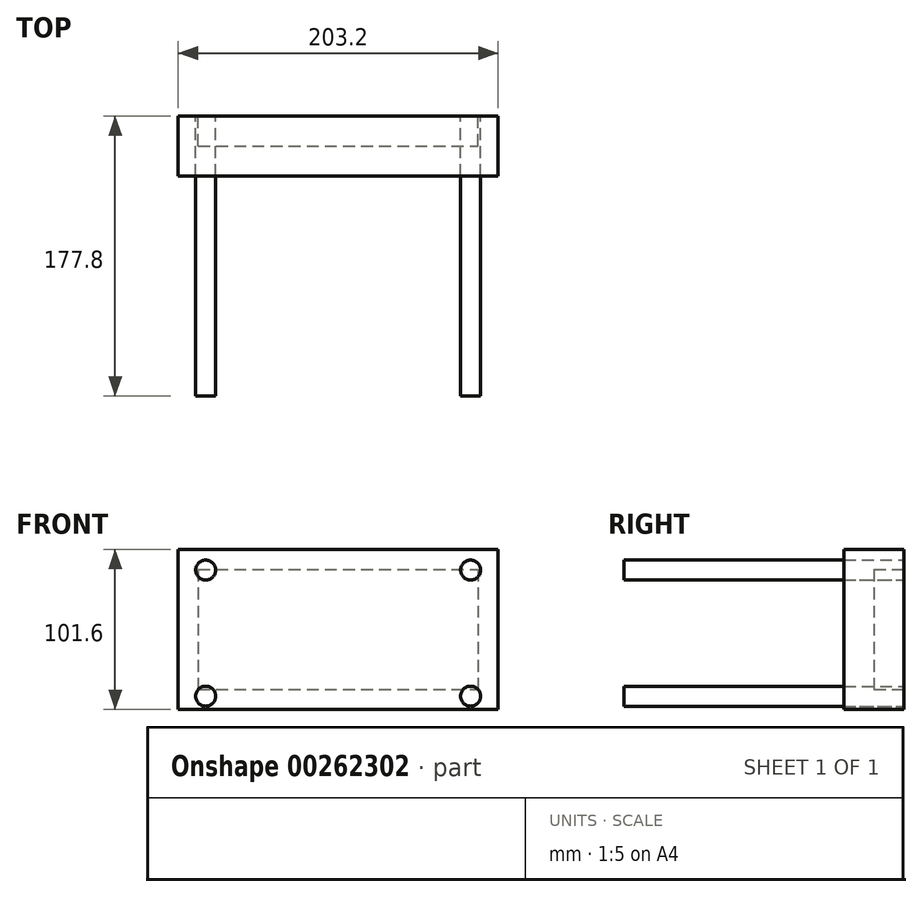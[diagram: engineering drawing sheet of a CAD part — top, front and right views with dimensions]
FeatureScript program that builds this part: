
annotation { "Feature Type Name" : "Feature", "Feature Type Description" : "" }
export const myFeature = defineFeature(function(context is Context, id is Id, definition is map)
    precondition{}
    {
        {
            var Q0;
            Q0=qCreatedBy(makeId("Front.planeOp"),FACE);
            var sketch = newSketch(context, id + "F0", { "sketchPlane" : qUnion([Q0])});
            skLineSegment(sketch, "E0.bottom", {"start": v(-101.6, 50.8) * mm, "end": v(101.6, 50.8) * mm});
            skLineSegment(sketch, "E0.top", {"start": v(-101.6, -50.8) * mm, "end": v(101.6, -50.8) * mm});
            skLineSegment(sketch, "E0.left", {"start": v(-101.6, 50.8) * mm, "end": v(-101.6, -50.8) * mm});
            skLineSegment(sketch, "E0.right", {"start": v(101.6, 50.8) * mm, "end": v(101.6, -50.8) * mm});
            skPoint(sketch, "E0.middle", {"position": v(0, 0) * mm});
            skCircle(sketch, "E1", {"center": v(84.1, 37.72) * mm, "radius": 6.35 * mm});
            skCircle(sketch, "E2", {"center": v(84.1, -42.37) * mm, "radius": 6.35 * mm});
            skCircle(sketch, "E3", {"center": v(-84.18, 37.72) * mm, "radius": 6.35 * mm});
            skCircle(sketch, "E4", {"center": v(-84.18, -42.37) * mm, "radius": 6.35 * mm});
            skSolve(sketch);
        }
        {
            var Q0;
            Q0=makeQuery(id+"F0.imprint","IMPRINT",FACE,{"disambiguationData":[TD([[makeQuery(id+"F0.imprint","IMPRINT",EDGE,{"derivedFrom":sQuery(id+"F0.wireOp",EDGE,"E0.bottom")}),-1.0]])]});
            var Q1;
            Q1=makeQuery(id+"F0.imprint","IMPRINT",FACE,{"disambiguationData":[TD([[makeQuery(id+"F0.imprint","IMPRINT",EDGE,{"derivedFrom":sQuery(id+"F0.wireOp",EDGE,"E2")}),1.0]])]});
            var Q2;
            Q2=makeQuery(id+"F0.imprint","IMPRINT",FACE,{"disambiguationData":[TD([[makeQuery(id+"F0.imprint","IMPRINT",EDGE,{"derivedFrom":sQuery(id+"F0.wireOp",EDGE,"E1")}),1.0]])]});
            var Q3;
            Q3=makeQuery(id+"F0.imprint","IMPRINT",FACE,{"disambiguationData":[TD([[makeQuery(id+"F0.imprint","IMPRINT",EDGE,{"derivedFrom":sQuery(id+"F0.wireOp",EDGE,"E3")}),1.0]])]});
            var Q4;
            Q4=makeQuery(id+"F0.imprint","IMPRINT",FACE,{"disambiguationData":[TD([[makeQuery(id+"F0.imprint","IMPRINT",EDGE,{"derivedFrom":sQuery(id+"F0.wireOp",EDGE,"E4")}),1.0]])]});
            extrude(context, id + "F1", {"entities" : qUnion([Q0, Q1, Q2, Q3, Q4]), "depth" : 38.1 * mm});
        }
        {
            var Q0;
            Q0=qCreatedBy(makeId("Front.planeOp"),FACE);
            var sketch = newSketch(context, id + "F2", { "sketchPlane" : qUnion([Q0])});
            skLineSegment(sketch, "E5.bottom", {"start": v(-88.9, 38.1) * mm, "end": v(88.9, 38.1) * mm});
            skLineSegment(sketch, "E5.top", {"start": v(-88.9, -38.1) * mm, "end": v(88.9, -38.1) * mm});
            skLineSegment(sketch, "E5.left", {"start": v(-88.9, 38.1) * mm, "end": v(-88.9, -38.1) * mm});
            skLineSegment(sketch, "E5.right", {"start": v(88.9, 38.1) * mm, "end": v(88.9, -38.1) * mm});
            skPoint(sketch, "E5.middle", {"position": v(0, 0) * mm});
            skSolve(sketch);
        }
        {
            var Q0;
            Q0 = qSketchRegion(id + "F2", true);
            extrude(context, id + "F3", {"entities" : qUnion([Q0]), "operationType" : NewBodyOperationType.REMOVE, "depth" : 19.05 * mm});
        }
        {
            var Q0;
            Q0=makeQuery(id+"F0.imprint","IMPRINT",FACE,{"disambiguationData":[TD([[makeQuery(id+"F0.imprint","IMPRINT",EDGE,{"derivedFrom":sQuery(id+"F0.wireOp",EDGE,"E4")}),1.0]])]});
            var Q1;
            Q1=makeQuery(id+"F0.imprint","IMPRINT",FACE,{"disambiguationData":[TD([[makeQuery(id+"F0.imprint","IMPRINT",EDGE,{"derivedFrom":sQuery(id+"F0.wireOp",EDGE,"E3")}),1.0]])]});
            var Q2;
            Q2=makeQuery(id+"F0.imprint","IMPRINT",FACE,{"disambiguationData":[TD([[makeQuery(id+"F0.imprint","IMPRINT",EDGE,{"derivedFrom":sQuery(id+"F0.wireOp",EDGE,"E2")}),1.0]])]});
            var Q3;
            Q3=makeQuery(id+"F0.imprint","IMPRINT",FACE,{"disambiguationData":[TD([[makeQuery(id+"F0.imprint","IMPRINT",EDGE,{"derivedFrom":sQuery(id+"F0.wireOp",EDGE,"E1")}),1.0]])]});
            extrude(context, id + "F4", {"entities" : qUnion([Q0, Q1, Q2, Q3]), "depth" : 177.8 * mm});
        }
    });
